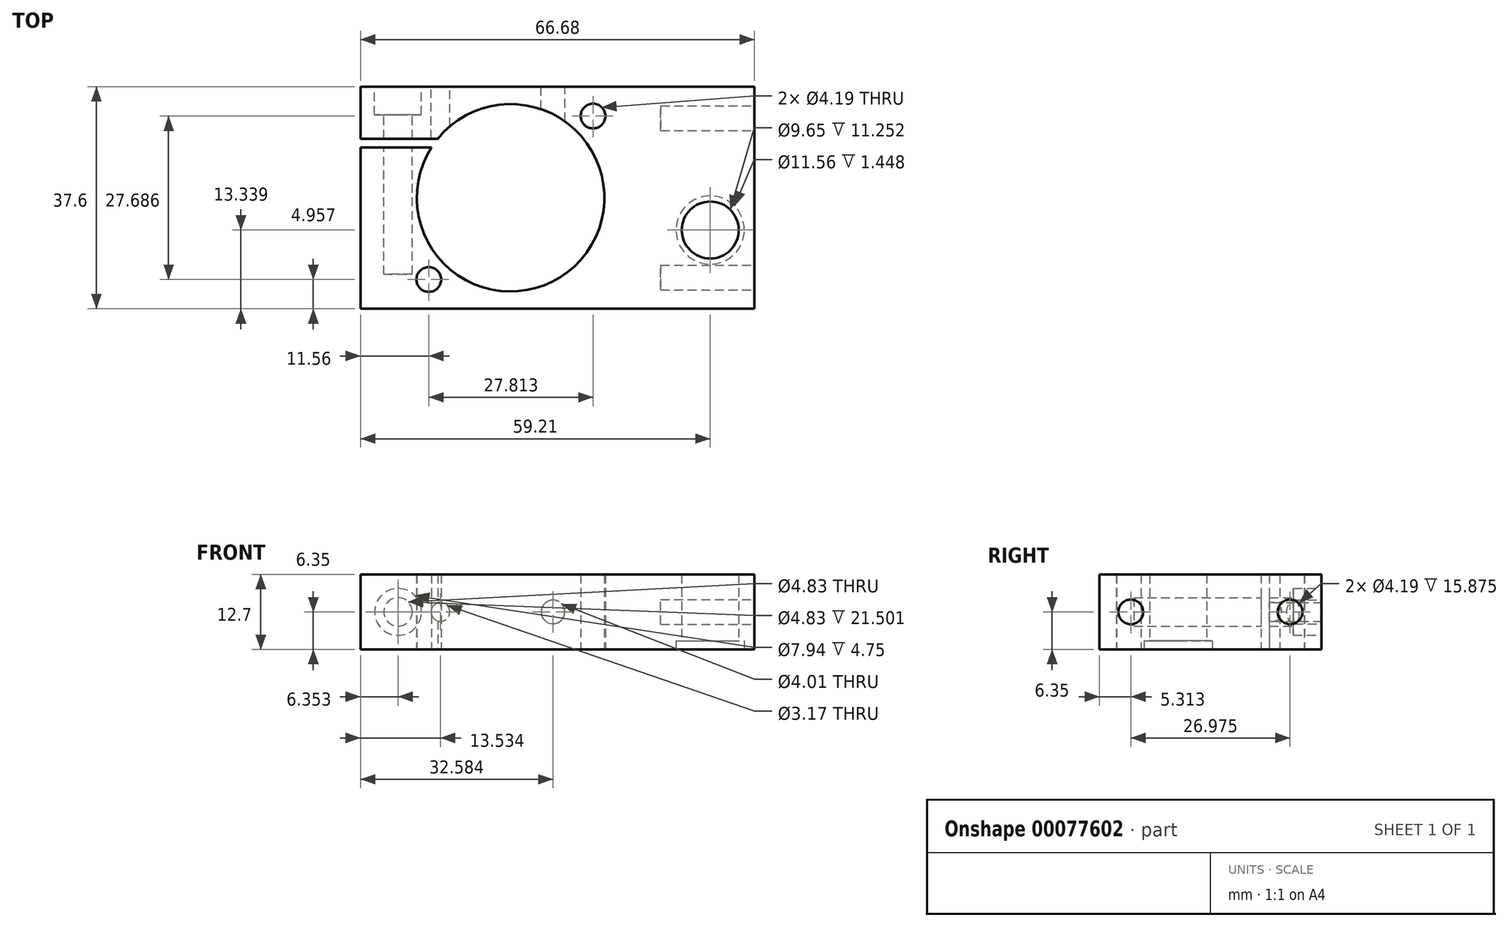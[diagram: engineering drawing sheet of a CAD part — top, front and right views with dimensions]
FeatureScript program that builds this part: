
annotation { "Feature Type Name" : "Feature", "Feature Type Description" : "" }
export const myFeature = defineFeature(function(context is Context, id is Id, definition is map)
    precondition{}
    {
        {
            var Q0;
            Q0=qCreatedBy(makeId("Top.planeOp"),FACE);
            var sketch = newSketch(context, id + "F0", { "sketchPlane" : qUnion([Q0])});
            skLineSegment(sketch, "E0.bottom", {"start": v(33.34, 18.8) * mm, "end": v(-33.34, 18.8) * mm});
            skLineSegment(sketch, "E0.top", {"start": v(33.34, -18.8) * mm, "end": v(-33.34, -18.8) * mm});
            skLineSegment(sketch, "E0.left", {"start": v(33.34, 18.8) * mm, "end": v(33.34, -18.8) * mm});
            skLineSegment(sketch, "E0.right", {"start": v(-33.34, 18.8) * mm, "end": v(-33.34, 10) * mm});
            skPoint(sketch, "E0.middle", {"position": v(0, 0) * mm});
            skArc(sketch, "E1", {"start": v(-21.32, 8.55) * mm, "mid": v(4.94, -9.29) * mm, "end": v(-20.27, 10) * mm});
            skCircle(sketch, "E2", {"center": v(25.87, -5.46) * mm, "radius": 4.83 * mm});
            skCircle(sketch, "E3", {"center": v(-21.78, -13.84) * mm, "radius": 2.1 * mm});
            skCircle(sketch, "E4", {"center": v(6.03, 13.84) * mm, "radius": 2.1 * mm});
            skLineSegment(sketch, "E5.bottom", {"start": v(-33.34, 10) * mm, "end": v(-20.27, 10) * mm});
            skLineSegment(sketch, "E5.top", {"start": v(-33.34, 8.55) * mm, "end": v(-21.32, 8.55) * mm});
            skPoint(sketch, "E5.middle", {"position": v(-25.3, 9.27) * mm});
            skLineSegment(sketch, "E6.trimOffspring", {"start": v(-33.34, 8.55) * mm, "end": v(-33.34, -18.8) * mm});
            skSolve(sketch);
        }
        {
            var Q0;
            Q0 = qSketchRegion(id + "F0", true);
            extrude(context, id + "F1", {"entities" : qUnion([Q0]), "depth" : 12.7 * mm});
        }
        {
            var Q0;
            Q0=makeQuery(id+"F1.opExtrude","SWEPT_FACE",FACE,{"disambiguationData":[OSD([sQuery(id+"F0.wireOp",EDGE,"E0.left")])]});
            var sketch = newSketch(context, id + "F2", { "sketchPlane" : qUnion([Q0])});
            skCircle(sketch, "E7", {"center": v(-13.49, 6.35) * mm, "radius": 2.1 * mm});
            skCircle(sketch, "E8", {"center": v(13.49, 6.35) * mm, "radius": 2.1 * mm});
            skSolve(sketch);
        }
        {
            var Q0;
            Q0 = qSketchRegion(id + "F2", true);
            extrude(context, id + "F3", {"entities" : qUnion([Q0]), "operationType" : NewBodyOperationType.REMOVE, "oppositeDirection" : true, "depth" : 15.88 * mm});
        }
        {
            var Q0;
            Q0=makeQuery(id+"F1.opExtrude","CAP_FACE",FACE,{"disambiguationData":[OSD([sQuery(id+"F0.wireOp",EDGE,"E0.bottom"),sQuery(id+"F0.wireOp",EDGE,"E0.top"),sQuery(id+"F0.wireOp",EDGE,"E0.left"),sQuery(id+"F0.wireOp",EDGE,"E0.right"),sQuery(id+"F0.wireOp",EDGE,"E1"),sQuery(id+"F0.wireOp",EDGE,"E2"),sQuery(id+"F0.wireOp",EDGE,"E3"),sQuery(id+"F0.wireOp",EDGE,"E4"),sQuery(id+"F0.wireOp",EDGE,"E5.bottom"),sQuery(id+"F0.wireOp",EDGE,"E5.top"),sQuery(id+"F0.wireOp",EDGE,"E6.trimOffspring")])],"isStart":true});
            var sketch = newSketch(context, id + "F4", { "sketchPlane" : qUnion([Q0])});
            skCircle(sketch, "E9", {"center": v(25.87, 5.46) * mm, "radius": 5.78 * mm});
            skSolve(sketch);
        }
        {
            var Q0;
            Q0 = qSketchRegion(id + "F4", true);
            extrude(context, id + "F5", {"entities" : qUnion([Q0]), "operationType" : NewBodyOperationType.REMOVE, "oppositeDirection" : true, "depth" : 1.45 * mm});
        }
        {
            var Q0;
            Q0=makeQuery(id+"F1.opExtrude","SWEPT_FACE",FACE,{"disambiguationData":[OSD([sQuery(id+"F0.wireOp",EDGE,"E0.bottom")])]});
            var sketch = newSketch(context, id + "F6", { "sketchPlane" : qUnion([Q0])});
            skCircle(sketch, "E10", {"center": v(26.99, 6.35) * mm, "radius": 2.41 * mm});
            skPoint(sketch, "E10.centerSnap0", {"position": v(33.34, 6.35) * mm});
            skSolve(sketch);
        }
        {
            var Q0;
            Q0 = qSketchRegion(id + "F6", true);
            extrude(context, id + "F7", {"entities" : qUnion([Q0]), "operationType" : NewBodyOperationType.REMOVE, "oppositeDirection" : true, "depth" : 31.75 * mm});
        }
        {
            var Q0;
            Q0=makeQuery(id+"F1.opExtrude","SWEPT_FACE",FACE,{"disambiguationData":[OSD([sQuery(id+"F0.wireOp",EDGE,"E0.bottom")])]});
            var sketch = newSketch(context, id + "F8", { "sketchPlane" : qUnion([Q0])});
            skCircle(sketch, "E11", {"center": v(26.99, 6.35) * mm, "radius": 3.97 * mm});
            skSolve(sketch);
        }
        {
            var Q0;
            Q0 = qSketchRegion(id + "F8", true);
            extrude(context, id + "F9", {"entities" : qUnion([Q0]), "operationType" : NewBodyOperationType.REMOVE, "oppositeDirection" : true, "depth" : 4.75 * mm});
        }
        {
            var Q0;
            Q0=makeQuery(id+"F1.opExtrude","SWEPT_FACE",FACE,{"disambiguationData":[OSD([sQuery(id+"F0.wireOp",EDGE,"E0.bottom")])]});
            var sketch = newSketch(context, id + "F10", { "sketchPlane" : qUnion([Q0])});
            skCircle(sketch, "E12", {"center": v(19.8, 6.35) * mm, "radius": 1.59 * mm});
            skPoint(sketch, "E12.centerSnap0", {"position": v(33.34, 6.35) * mm});
            skCircle(sketch, "E13", {"center": v(0.76, 6.35) * mm, "radius": 2 * mm});
            skSolve(sketch);
        }
        {
            var Q0;
            Q0 = qSketchRegion(id + "F10", true);
            extrude(context, id + "F11", {"entities" : qUnion([Q0]), "operationType" : NewBodyOperationType.REMOVE, "oppositeDirection" : true, "depth" : 9.52 * mm});
        }
    });
